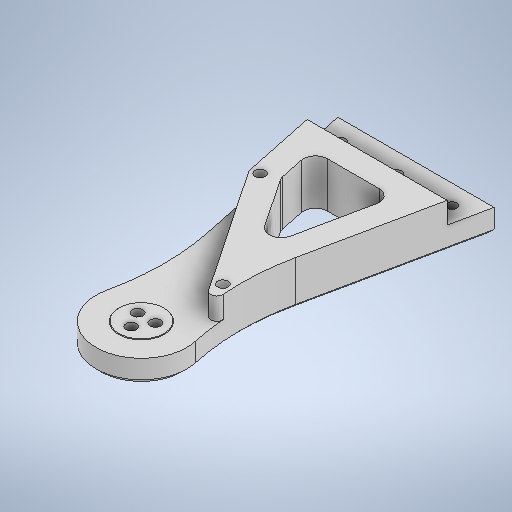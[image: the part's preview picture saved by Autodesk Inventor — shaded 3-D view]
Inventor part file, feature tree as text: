
AUTODESK INVENTOR PART (.ipt)
format: ipt  version: 2025.2 (Build 292293000, 293)  size: 794,624 bytes
history: native  units: mm
features: extrude x12, sketch x12, other x9, reference x7, projected_geometry x4, chamfer x2, fillet x1
ambient origin geometry x8: Origin, YZ Plane, XZ Plane, XY Plane, X Axis, Y Axis, Z Axis, Center Point
bodies: Solid1 (feature_tree)
feature tree (47):
  other  "motion_thigh_bot"
  extrude  "Extrusion1"  Depth=75.0mm
  extrude  "Extrusion4"  Depth=47.0mm
  extrude  "Extrusion5"  Depth=4.0mm
  extrude  "Extrusion6"  Depth=16.256841mm
  extrude  "Extrusion7"  Depth=35.0mm
  extrude  "Extrusion8"  Depth=48.150251mm
  extrude  "Extrusion11"  Depth=48.150251mm
  chamfer  "Chamfer1"  Distance=8.128925mm
  extrude  "Extrusion16"  Depth=2.0mm
  extrude  "Extrusion17"  TaperAngle=0.0deg  [1 undecoded]
  extrude  "Extrusion18"  Depth=16.256841mm
  extrude  "Extrusion19"  Depth=2.0mm
  fillet  "Fillet2"  Radius=16.256841mm
  extrude  "Extrusion20"  Depth=10.0mm TaperAngle=0.0deg
  chamfer  "Chamfer2"  [1 undecoded]
  sketch  "Sketch1"  dims[d0=150.0mm d1=75.0mm]
  sketch  "Sketch4"  dims[d22=38.0mm d33=47.0mm]
  reference  "Reference1"
  sketch  "Sketch5"  dims[d34=4.0mm d35=12.533523mm]
  sketch  "Sketch6"  dims[d36=12.533523mm d37=16.256841mm]
  sketch  "Sketch7"  dims[d38=35.0mm d39=35.0mm]
  reference  "Reference2"
  sketch  "Sketch8"  dims[d40=0.0mm d41=48.150251mm]
  sketch  "Sketch11"  dims[d42=0.0mm d43=48.150251mm]
  reference  "Reference4"
  reference  "Reference5"
  sketch  "Sketch17"  dims[d44=0.0mm]
  reference  "Reference9"
  reference  "Reference10"
  projected_geometry  "Projected Loop2"
  sketch  "Sketch18"  dims[d45=8.128925mm]
  reference  "Reference11"
  projected_geometry  "Projected Loop3"
  sketch  "Sketch19"  dims[d46=10.137333mm]
  sketch  "Sketch20"  dims[d47=8.128925mm]
  projected_geometry  "Projected Loop4"
  sketch  "Sketch21"  dims[d48=21.537769mm d49=8.128925mm d50=32.938205mm d51=0.0mm d52=16.256841mm d53=38.001454mm d54=16.256841mm d55=10.0mm d56=0.0mm d67=0.0mm d68=0.0mm d69=4.45mm d70=4.45mm d71=4.45mm d72=6.0mm d73=0.0mm d74=6.0mm d75=0.0mm d76=10.0mm d77=0.0mm d80=100.0mm d81=10.0mm d82=0.0mm d93=0.0mm d94=0.0mm d95=2.0mm d96=2.0mm d97=45.0deg d113=9.0mm d114=0.0mm d117=7.05mm d118=9.0mm d119=0.0mm d120=4.45mm d121=7.05mm d122=4.45mm d123=9.5mm d124=0.0mm d125=10.0mm d126=10.0mm d127=0.0mm d128=5.0mm d129=17.0mm d130=0.85mm d131=0.2mm d132=0.0mm d133=0.2mm d134=2.0mm d135=45.0deg]
  projected_geometry  "Projected Loop5"
  parser-record x2  (decoder bookkeeping rows leaked as tree rows — omitted from the tree; the rows remain in map.json)
  other  "leg_articulation_assembly.iam"
  other  "motion_thigh_top:1"
  other  "Big_drum:1"
  other  "WBR.iam"
  other  "leg_wheel:1"
  other  "leg_extend:1"
note: 2 required parameter values undecoded (feature->parameter linkage not recoverable at this tier; creation-order binding heuristic only, values carry confidence <= 0.55)
note: 2 file-system paths scrubbed to <path> (originals preserved in map.json)
